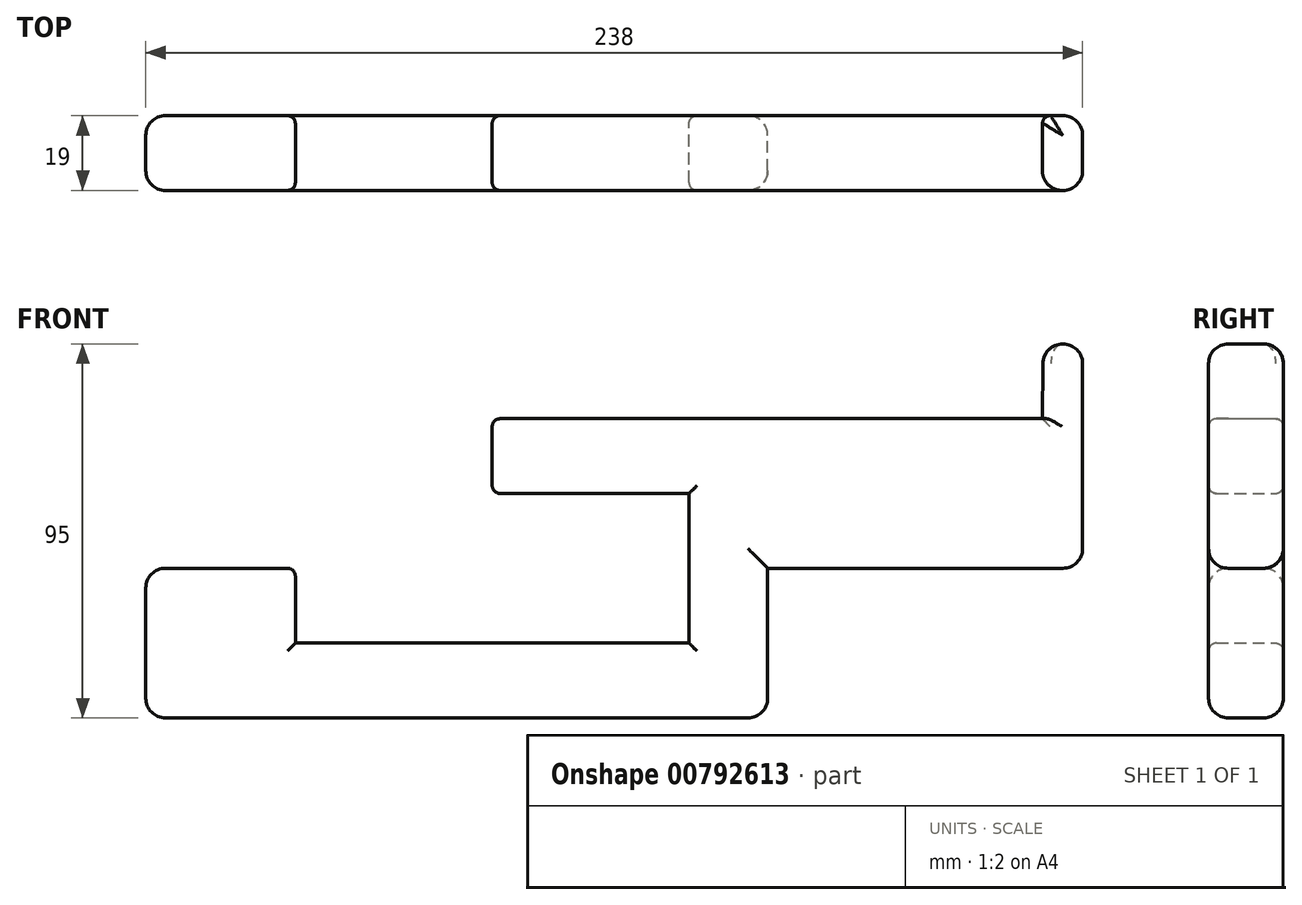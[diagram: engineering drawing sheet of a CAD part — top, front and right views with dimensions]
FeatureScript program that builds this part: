
annotation { "Feature Type Name" : "Feature", "Feature Type Description" : "" }
export const myFeature = defineFeature(function(context is Context, id is Id, definition is map)
    precondition{}
    {
        {
            var Q0;
            Q0=qCreatedBy(makeId("Front.planeOp"),FACE);
            var sketch = newSketch(context, id + "F0", { "sketchPlane" : qUnion([Q0])});
            skLineSegment(sketch, "E0", {"start": v(0, 0) * mm, "end": v(0, -38) * mm});
            skLineSegment(sketch, "E1", {"start": v(-80, -76) * mm, "end": v(-238, -76) * mm});
            skLineSegment(sketch, "E2", {"start": v(-238, -76) * mm, "end": v(-238, -38) * mm});
            skLineSegment(sketch, "E3", {"start": v(-238, -38) * mm, "end": v(-200, -38) * mm});
            skLineSegment(sketch, "E4", {"start": v(-200, -38) * mm, "end": v(-200, -57) * mm});
            skLineSegment(sketch, "E5", {"start": v(-200, -57) * mm, "end": v(-100, -57) * mm});
            skLineSegment(sketch, "E6", {"start": v(-100, -57) * mm, "end": v(-100, -19) * mm});
            skLineSegment(sketch, "E7", {"start": v(-100, -19) * mm, "end": v(-150, -19) * mm});
            skLineSegment(sketch, "E8", {"start": v(-150, -19) * mm, "end": v(-150, 0) * mm});
            skLineSegment(sketch, "E9", {"start": v(-150, 0) * mm, "end": v(-10.22, 0) * mm});
            skPoint(sketch, "E10", {"position": v(-80, -76) * mm});
            skPoint(sketch, "E11", {"position": v(0, -38) * mm});
            skLineSegment(sketch, "E12", {"start": v(-80, -76) * mm, "end": v(-80, -38) * mm});
            skLineSegment(sketch, "E13", {"start": v(-80, -38) * mm, "end": v(0, -38) * mm});
            skPoint(sketch, "E14", {"position": v(-10.22, 0) * mm});
            skLineSegment(sketch, "E15", {"start": v(0, 0) * mm, "end": v(0, 19) * mm});
            skLineSegment(sketch, "E16", {"start": v(0, 19) * mm, "end": v(-10, 19) * mm});
            skLineSegment(sketch, "E17", {"start": v(-10, 19) * mm, "end": v(-10.22, 0) * mm});
            skSolve(sketch);
        }
        {
            var Q0;
            Q0 = qSketchRegion(id + "F0", true);
            extrude(context, id + "F1", {"entities" : qUnion([Q0]), "depth" : 19 * mm, "offsetDistance" : 25 * mm});
        }
        {
            var Q0;
            Q0=makeQuery(id+"F1.opExtrude","SWEPT_EDGE",EDGE,{"disambiguationData":[OSD([sQuery(id+"F0.wireOp",EDGE,"E2"),sQuery(id+"F0.wireOp",EDGE,"E3")])]});
            var Q1;
            Q1=makeQuery(id+"F1.opExtrude","CAP_EDGE",EDGE,{"disambiguationData":[OSD([sQuery(id+"F0.wireOp",EDGE,"E2")])],"isStart":false});
            var Q2;
            Q2=makeQuery(id+"F1.opExtrude","CAP_EDGE",EDGE,{"disambiguationData":[OSD([sQuery(id+"F0.wireOp",EDGE,"E1")])],"isStart":false});
            var Q3;
            Q3=makeQuery(id+"F1.opExtrude","SWEPT_EDGE",EDGE,{"disambiguationData":[OSD([sQuery(id+"F0.wireOp",EDGE,"E1"),sQuery(id+"F0.wireOp",EDGE,"E12")])]});
            var Q4;
            Q4=makeQuery(id+"F1.opExtrude","CAP_EDGE",EDGE,{"disambiguationData":[OSD([sQuery(id+"F0.wireOp",EDGE,"E13")])],"isStart":false});
            var Q5;
            Q5=makeQuery(id+"F1.opExtrude","CAP_EDGE",EDGE,{"disambiguationData":[OSD([sQuery(id+"F0.wireOp",EDGE,"E12")])],"isStart":false});
            var Q6;
            Q6=makeQuery(id+"F1.opExtrude","SWEPT_EDGE",EDGE,{"disambiguationData":[OSD([sQuery(id+"F0.wireOp",EDGE,"E0"),sQuery(id+"F0.wireOp",EDGE,"E13")])]});
            var Q7;
            Q7=makeQuery(id+"F1.opExtrude","CAP_EDGE",EDGE,{"disambiguationData":[OSD([sQuery(id+"F0.wireOp",EDGE,"E0"),sQuery(id+"F0.wireOp",EDGE,"E15")])],"isStart":false});
            var Q8;
            Q8=makeQuery(id+"F1.opExtrude","SWEPT_EDGE",EDGE,{"disambiguationData":[OSD([sQuery(id+"F0.wireOp",EDGE,"E15"),sQuery(id+"F0.wireOp",EDGE,"E16")])]});
            var Q9;
            Q9=makeQuery(id+"F1.opExtrude","CAP_EDGE",EDGE,{"disambiguationData":[OSD([sQuery(id+"F0.wireOp",EDGE,"E16")])],"isStart":false});
            fillet(context, id + "F2", {"entities" : qUnion([Q0, Q1, Q2, Q3, Q4, Q5, Q6, Q7, Q8, Q9]), "radius" : 5 * mm, "tangentPropagation" : true, "allowEdgeOverflow" : false});
        }
        {
            var Q0;
            Q0=makeQuery(id+"F1.opExtrude","CAP_EDGE",EDGE,{"disambiguationData":[OSD([sQuery(id+"F0.wireOp",EDGE,"E0"),sQuery(id+"F0.wireOp",EDGE,"E15")])],"isStart":true});
            var Q1;
            Q1=makeQuery(id+"F1.opExtrude","CAP_EDGE",EDGE,{"disambiguationData":[OSD([sQuery(id+"F0.wireOp",EDGE,"E1")])],"isStart":true});
            var Q2;
            Q2=makeQuery(id+"F1.opExtrude","CAP_EDGE",EDGE,{"disambiguationData":[OSD([sQuery(id+"F0.wireOp",EDGE,"E2")])],"isStart":true});
            var Q3;
            Q3=makeQuery(id+"F1.opExtrude","SWEPT_EDGE",EDGE,{"disambiguationData":[OSD([sQuery(id+"F0.wireOp",EDGE,"E1"),sQuery(id+"F0.wireOp",EDGE,"E2")])]});
            var Q4;
            Q4=makeQuery(id+"F1.opExtrude","SWEPT_EDGE",EDGE,{"disambiguationData":[OSD([sQuery(id+"F0.wireOp",EDGE,"E16"),sQuery(id+"F0.wireOp",EDGE,"E17")])]});
            fillet(context, id + "F3", {"entities" : qUnion([Q0, Q1, Q2, Q3, Q4]), "radius" : 5 * mm, "tangentPropagation" : true, "allowEdgeOverflow" : false});
        }
        {
            var Q0;
            Q0=makeQuery(id+"F1.opExtrude","CAP_EDGE",EDGE,{"disambiguationData":[OSD([sQuery(id+"F0.wireOp",EDGE,"E9")])],"isStart":true});
            var Q1;
            Q1=makeQuery(id+"F1.opExtrude","CAP_EDGE",EDGE,{"disambiguationData":[OSD([sQuery(id+"F0.wireOp",EDGE,"E7")])],"isStart":true});
            var Q2;
            Q2=makeQuery(id+"F1.opExtrude","CAP_EDGE",EDGE,{"disambiguationData":[OSD([sQuery(id+"F0.wireOp",EDGE,"E6")])],"isStart":true});
            var Q3;
            Q3=makeQuery(id+"F1.opExtrude","CAP_EDGE",EDGE,{"disambiguationData":[OSD([sQuery(id+"F0.wireOp",EDGE,"E5")])],"isStart":true});
            var Q4;
            Q4=makeQuery(id+"F1.opExtrude","SWEPT_EDGE",EDGE,{"disambiguationData":[OSD([sQuery(id+"F0.wireOp",EDGE,"E7"),sQuery(id+"F0.wireOp",EDGE,"E8")])]});
            var Q5;
            Q5=makeQuery(id+"F1.opExtrude","SWEPT_EDGE",EDGE,{"disambiguationData":[OSD([sQuery(id+"F0.wireOp",EDGE,"E8"),sQuery(id+"F0.wireOp",EDGE,"E9")])]});
            var Q6;
            Q6=makeQuery(id+"F1.opExtrude","CAP_EDGE",EDGE,{"disambiguationData":[OSD([sQuery(id+"F0.wireOp",EDGE,"E9")])],"isStart":false});
            var Q7;
            Q7=makeQuery(id+"F1.opExtrude","CAP_EDGE",EDGE,{"disambiguationData":[OSD([sQuery(id+"F0.wireOp",EDGE,"E8")])],"isStart":false});
            var Q8;
            Q8=makeQuery(id+"F1.opExtrude","CAP_EDGE",EDGE,{"disambiguationData":[OSD([sQuery(id+"F0.wireOp",EDGE,"E5")])],"isStart":false});
            var Q9;
            Q9=makeQuery(id+"F1.opExtrude","CAP_EDGE",EDGE,{"disambiguationData":[OSD([sQuery(id+"F0.wireOp",EDGE,"E6")])],"isStart":false});
            var Q10;
            Q10=makeQuery(id+"F1.opExtrude","CAP_EDGE",EDGE,{"disambiguationData":[OSD([sQuery(id+"F0.wireOp",EDGE,"E4")])],"isStart":false});
            var Q11;
            Q11=makeQuery(id+"F1.opExtrude","SWEPT_EDGE",EDGE,{"disambiguationData":[OSD([sQuery(id+"F0.wireOp",EDGE,"E3"),sQuery(id+"F0.wireOp",EDGE,"E4")])]});
            var Q12;
            Q12=makeQuery(id+"F1.opExtrude","CAP_EDGE",EDGE,{"disambiguationData":[OSD([sQuery(id+"F0.wireOp",EDGE,"E8")])],"isStart":true});
            fillet(context, id + "F4", {"entities" : qUnion([Q0, Q1, Q2, Q3, Q4, Q5, Q6, Q7, Q8, Q9, Q10, Q11, Q12]), "radius" : 2 * mm, "tangentPropagation" : true, "allowEdgeOverflow" : false});
        }
        {
            var Q0;
            Q0=makeQuery(id+"F1.opExtrude","CAP_EDGE",EDGE,{"disambiguationData":[OSD([sQuery(id+"F0.wireOp",EDGE,"E17")])],"isStart":true});
            fillet(context, id + "F5", {"entities" : qUnion([Q0]), "radius" : 2 * mm, "tangentPropagation" : true, "allowEdgeOverflow" : false});
        }
        {
            var Q0;
            Q0=makeQuery(id+"F1.opExtrude","CAP_EDGE",EDGE,{"disambiguationData":[OSD([sQuery(id+"F0.wireOp",EDGE,"E3")])],"isStart":false});
            fillet(context, id + "F6", {"entities" : qUnion([Q0]), "radius" : 5 * mm, "tangentPropagation" : true, "allowEdgeOverflow" : false});
        }
        {
            var Q0;
            Q0=makeQuery(id+"F1.opExtrude","CAP_EDGE",EDGE,{"disambiguationData":[OSD([sQuery(id+"F0.wireOp",EDGE,"E7")])],"isStart":false});
            fillet(context, id + "F7", {"entities" : qUnion([Q0]), "radius" : 2 * mm, "tangentPropagation" : true, "allowEdgeOverflow" : false});
        }
    });
